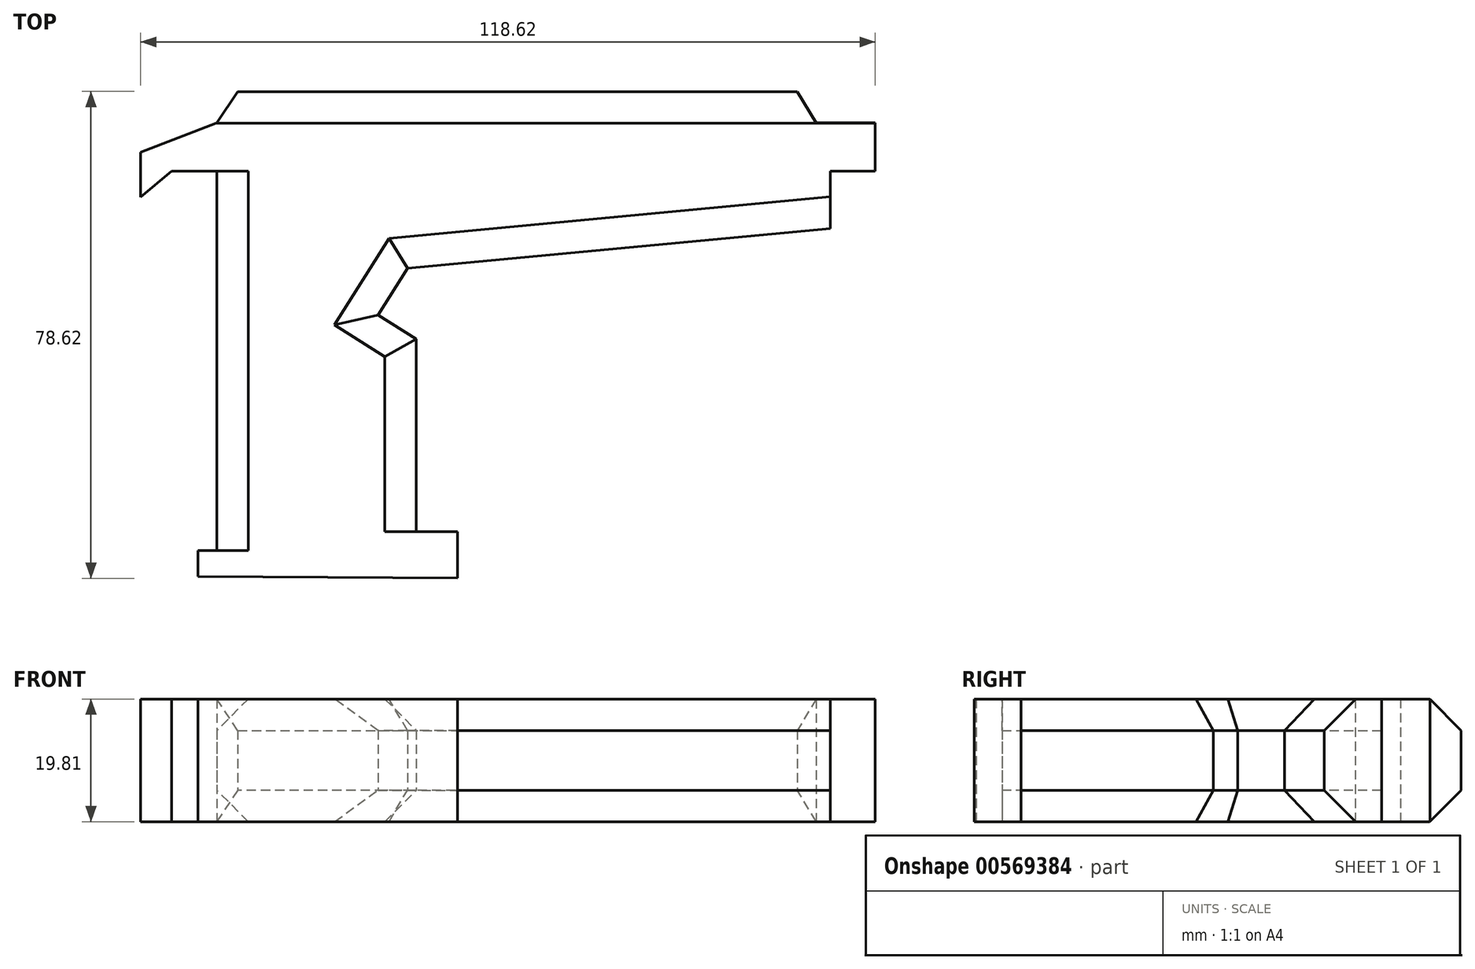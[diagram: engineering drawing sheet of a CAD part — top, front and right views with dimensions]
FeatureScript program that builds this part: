
annotation { "Feature Type Name" : "Feature", "Feature Type Description" : "" }
export const myFeature = defineFeature(function(context is Context, id is Id, definition is map)
    precondition{}
    {
        {
            var Q0;
            Q0=qCreatedBy(makeId("Top.planeOp"),FACE);
            var sketch = newSketch(context, id + "F0", { "sketchPlane" : qUnion([Q0])});
            skLineSegment(sketch, "E0", {"start": v(-58.6, -49.8) * mm, "end": v(-58.6, -45.6) * mm});
            skLineSegment(sketch, "E1", {"start": v(-58.6, -45.6) * mm, "end": v(-55.53, -45.6) * mm});
            skLineSegment(sketch, "E2", {"start": v(-55.53, -45.6) * mm, "end": v(-55.53, 15.67) * mm});
            skLineSegment(sketch, "E3", {"start": v(-55.53, 15.67) * mm, "end": v(-62.8, 15.67) * mm});
            skLineSegment(sketch, "E4", {"start": v(-62.8, 15.67) * mm, "end": v(-67.84, 11.47) * mm});
            skLineSegment(sketch, "E5", {"start": v(-67.84, 11.47) * mm, "end": v(-67.84, 18.74) * mm});
            skLineSegment(sketch, "E6", {"start": v(-67.84, 18.74) * mm, "end": v(-55.53, 23.5) * mm});
            skLineSegment(sketch, "E7", {"start": v(-55.53, 23.5) * mm, "end": v(-52.17, 28.54) * mm});
            skLineSegment(sketch, "E8", {"start": v(-52.17, 28.54) * mm, "end": v(38.19, 28.54) * mm});
            skLineSegment(sketch, "E9", {"start": v(38.19, 28.54) * mm, "end": v(41.26, 23.5) * mm});
            skLineSegment(sketch, "E10", {"start": v(41.26, 23.5) * mm, "end": v(50.78, 23.5) * mm});
            skLineSegment(sketch, "E11", {"start": v(50.78, 23.5) * mm, "end": v(50.78, 15.67) * mm});
            skLineSegment(sketch, "E12", {"start": v(50.78, 15.67) * mm, "end": v(43.5, 15.67) * mm});
            skLineSegment(sketch, "E13", {"start": v(43.5, 15.67) * mm, "end": v(43.5, 6.43) * mm});
            skLineSegment(sketch, "E14", {"start": v(43.5, 6.43) * mm, "end": v(-24.76, 0) * mm});
            skLineSegment(sketch, "E15", {"start": v(-24.76, 0) * mm, "end": v(-29.51, -7.55) * mm});
            skLineSegment(sketch, "E16", {"start": v(-29.51, -7.55) * mm, "end": v(-23.31, -11.46) * mm});
            skLineSegment(sketch, "E17", {"start": v(-23.31, -11.46) * mm, "end": v(-23.31, -25.74) * mm});
            skLineSegment(sketch, "E18", {"start": v(-23.31, -25.74) * mm, "end": v(-23.31, -42.52) * mm});
            skLineSegment(sketch, "E19", {"start": v(-23.31, -42.52) * mm, "end": v(-16.65, -42.52) * mm});
            skLineSegment(sketch, "E20", {"start": v(-16.65, -42.52) * mm, "end": v(-16.65, -50.08) * mm});
            skLineSegment(sketch, "E21", {"start": v(-16.65, -50.08) * mm, "end": v(-58.6, -49.8) * mm});
            skSolve(sketch);
        }
        {
            var Q0;
            Q0=makeQuery(id+"F0.imprint","IMPRINT",FACE,{"disambiguationData":[TD([[makeQuery(id+"F0.imprint","IMPRINT",EDGE,{"derivedFrom":sQuery(id+"F0.wireOp",EDGE,"E0")}),-1.0]])]});
            extrude(context, id + "F1", {"entities" : qUnion([Q0]), "depth" : 19.8 * mm, "offsetDistance" : 25.4 * mm});
        }
        {
            var Q0;
            Q0=makeQuery(id+"F1.opExtrude","CAP_EDGE",EDGE,{"disambiguationData":[OSD([sQuery(id+"F0.wireOp",EDGE,"E8")])],"isStart":false});
            var Q1;
            Q1=makeQuery(id+"F1.opExtrude","CAP_EDGE",EDGE,{"disambiguationData":[OSD([sQuery(id+"F0.wireOp",EDGE,"E14")])],"isStart":false});
            var Q2;
            Q2=makeQuery(id+"F1.opExtrude","CAP_EDGE",EDGE,{"disambiguationData":[OSD([sQuery(id+"F0.wireOp",EDGE,"E2")])],"isStart":false});
            var Q3;
            Q3=makeQuery(id+"F1.opExtrude","CAP_EDGE",EDGE,{"disambiguationData":[OSD([sQuery(id+"F0.wireOp",EDGE,"E17"),sQuery(id+"F0.wireOp",EDGE,"E18")])],"isStart":false});
            var Q4;
            Q4=makeQuery(id+"F1.opExtrude","CAP_EDGE",EDGE,{"disambiguationData":[OSD([sQuery(id+"F0.wireOp",EDGE,"E16")])],"isStart":false});
            var Q5;
            Q5=makeQuery(id+"F1.opExtrude","CAP_EDGE",EDGE,{"disambiguationData":[OSD([sQuery(id+"F0.wireOp",EDGE,"E15")])],"isStart":false});
            chamfer(context, id + "F2", {"entities" : qUnion([Q0, Q1, Q2, Q3, Q4, Q5]), "width" : 5.08 * mm, "tangentPropagation" : true});
        }
        {
            var Q0;
            Q0=makeQuery(id+"F1.opExtrude","CAP_EDGE",EDGE,{"disambiguationData":[OSD([sQuery(id+"F0.wireOp",EDGE,"E2")])],"isStart":true});
            var Q1;
            Q1=makeQuery(id+"F1.opExtrude","CAP_EDGE",EDGE,{"disambiguationData":[OSD([sQuery(id+"F0.wireOp",EDGE,"E8")])],"isStart":true});
            var Q2;
            Q2=makeQuery(id+"F1.opExtrude","CAP_EDGE",EDGE,{"disambiguationData":[OSD([sQuery(id+"F0.wireOp",EDGE,"E14")])],"isStart":true});
            var Q3;
            Q3=makeQuery(id+"F1.opExtrude","CAP_EDGE",EDGE,{"disambiguationData":[OSD([sQuery(id+"F0.wireOp",EDGE,"E17"),sQuery(id+"F0.wireOp",EDGE,"E18")])],"isStart":true});
            var Q4;
            Q4=makeQuery(id+"F1.opExtrude","CAP_EDGE",EDGE,{"disambiguationData":[OSD([sQuery(id+"F0.wireOp",EDGE,"E16")])],"isStart":true});
            var Q5;
            Q5=makeQuery(id+"F1.opExtrude","CAP_EDGE",EDGE,{"disambiguationData":[OSD([sQuery(id+"F0.wireOp",EDGE,"E15")])],"isStart":true});
            chamfer(context, id + "F3", {"entities" : qUnion([Q0, Q1, Q2, Q3, Q4, Q5]), "width" : 5.08 * mm, "tangentPropagation" : true});
        }
    });
